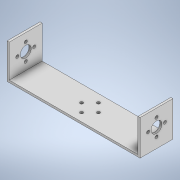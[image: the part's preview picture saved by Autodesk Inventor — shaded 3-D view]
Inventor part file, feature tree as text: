
AUTODESK INVENTOR PART (.ipt)
format: ipt  version: 2020 (Build 240168000, 168)  size: 152,064 bytes
history: native  units: in
note: dims shown in document units (in); Inventor stores cm internally (conversion verified against a paired STEP export)
features: extrude x4, sketch x4
ambient origin geometry x8: Origin, YZ Plane, XZ Plane, XY Plane, X Axis, Y Axis, Z Axis, Center Point
bodies: Solid1 (feature_tree)
feature tree (8):
  extrude  "Extrusion1"  Depth=1.5in
  sketch  "Sketch3"  dims[d2=0.1in d3=0.0in d7=0.77in]
  extrude  "Extrusion3"  Depth=0.1in
  extrude  "Extrusion4"  Depth=1.5in TaperAngle=0.0deg
  extrude  "Extrusion5"  Depth=0.1in
  sketch  "Sketch1"  dims[d0=6.063in d1=1.5in]
  sketch  "Sketch4"  dims[d12=0.5in d13=1.5in d14=0.0in]
  sketch  "Sketch5"  dims[d15=8.0in d16=0.0in d17=0.1in d18=0.77in d19=0.141in d20=0.141in d21=0.141in d22=0.141in d23=8.0in d24=0.0in]
